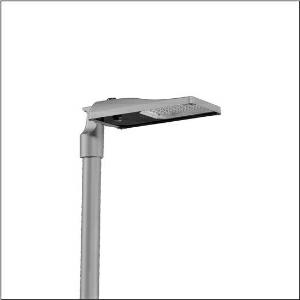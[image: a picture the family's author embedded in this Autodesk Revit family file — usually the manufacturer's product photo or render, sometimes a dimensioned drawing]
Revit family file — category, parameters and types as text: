
# Revit family: streetlight_sl_31_mini___st1_0a_5xh2d71t08ja_f6e8
name_source: partatom
category: Lighting Fixtures
units: mm (PartAtom-declared; Revit-internal decimal feet)

## family parameters
Cut with Voids When Loaded = No
Host = Face
Light Source = No
Part Type = Normal
Room Calculation Point = No
Round Connector Dimension = Use Diameter
Shared = No

## types (1)
- --- (1 x LED, 10110 lm, 82.5 W, 2200K)
    Apparent Load = 83 VA
    CIE Flux Codes = 40 73 97 100 100
    Color Rendering = 70
    Color Temperature = 2200K
    Default Elevation = 1800 mm
    Description = Streetlight SL 31 mini D4i, Desk-Remote mast luminaire for post-top, side-entry; light control with lens of PMMA; light distribution: ST1.0a, direct asymmetric distribution, for standard-compliant lighting for roads and squares; LED: luminous flux: 10.110lm, light colour: 722, colour temperature: 2200K; luminous efficacy: 122,5lm/W; control: pre-setting: logarithmic dimming characteristic, flexible luminous flux parameterisation, time-dependent luminous flux control, constant luminous flux control, power reduction, intelligent temperature release in ECG and LED module, overheat protection; luminaire housing, of diecast aluminium, Siteco® metallic grey (DB 702S), corrosivity category C5 high according to DIN EN ISO 12944; cover of toughened safety glass, transparent, mast flange of diecast aluminium, Siteco® metallic grey (DB 702S), spigot size: 76/60mm, mast flange included unmounted; with cable H07RN-F 2x 1.5mm², cable length: 10,5m, connection cable pre-assembled; mains connection: 220..240V, AC, 50/60Hz; power consumption (at start of service life): 82,5W / (at end of service life): 90,1W / (with reduced operation 50%): 36,5W; protection rating (complete): IP66; insulation class (complete): insulation class II (safety insulation); impact resistance: IK09; certification: CE, ENEC, ENEC+, VDE, UKCA, ZD4i; permissible operating ambient temperature for outdoor applications: -40..+50°C; packaging unit: 1 piece

Light Distribution: ST1.0a
    Height = 76 mm
    Lamp = 1 x LED
    Lamp Light Flux = 10110 lm
    Lamp Power = 82.5 W
    Lamp count = 1
    Length = 547 mm
    Luminous efficacy = 123 lm/W
    Manufacturer = Siteco
    ModVariant = No
    Model = 5XH2D71T08JA
    Number of Poles = 1
    OnlyDefault = Yes
    Power Factor = 1
    Product Name = Streetlight SL 31 mini | ST1.0a
    Product group = mast luminaire | pylon top
    ProductGroupID = 6100
    Protection Class = Protection class II
    Protection Degree = IP 66
    RLX_Detail_Level = 1
    RLX_Emergency_Light_Flux = 0 lm
    RLX_Emergency_Type = 0
    RLX_Emergency_Type_DB = No
    RlxData = <blob elided: 39841 chars, md5=135efe04>
    Socket = socket
    Standby Power = 0 W
    System Light Flux = 10110 lm
    System Power = 83 W
    Type Comments = factory setting: luminous flux: 100 % | dim-lin: 254 | 870 mA
    Type Image = l_1300332.jpg
    URL = http://relux.com
    VarID = @adj_047694
    Voltage = 0 V
    Weight = 0.00 kg
    Width = 265 mm

## geometry (parser evidence)
native form markers: Blend x4, Sweep x11
no freeform markers — native parametric forms only
